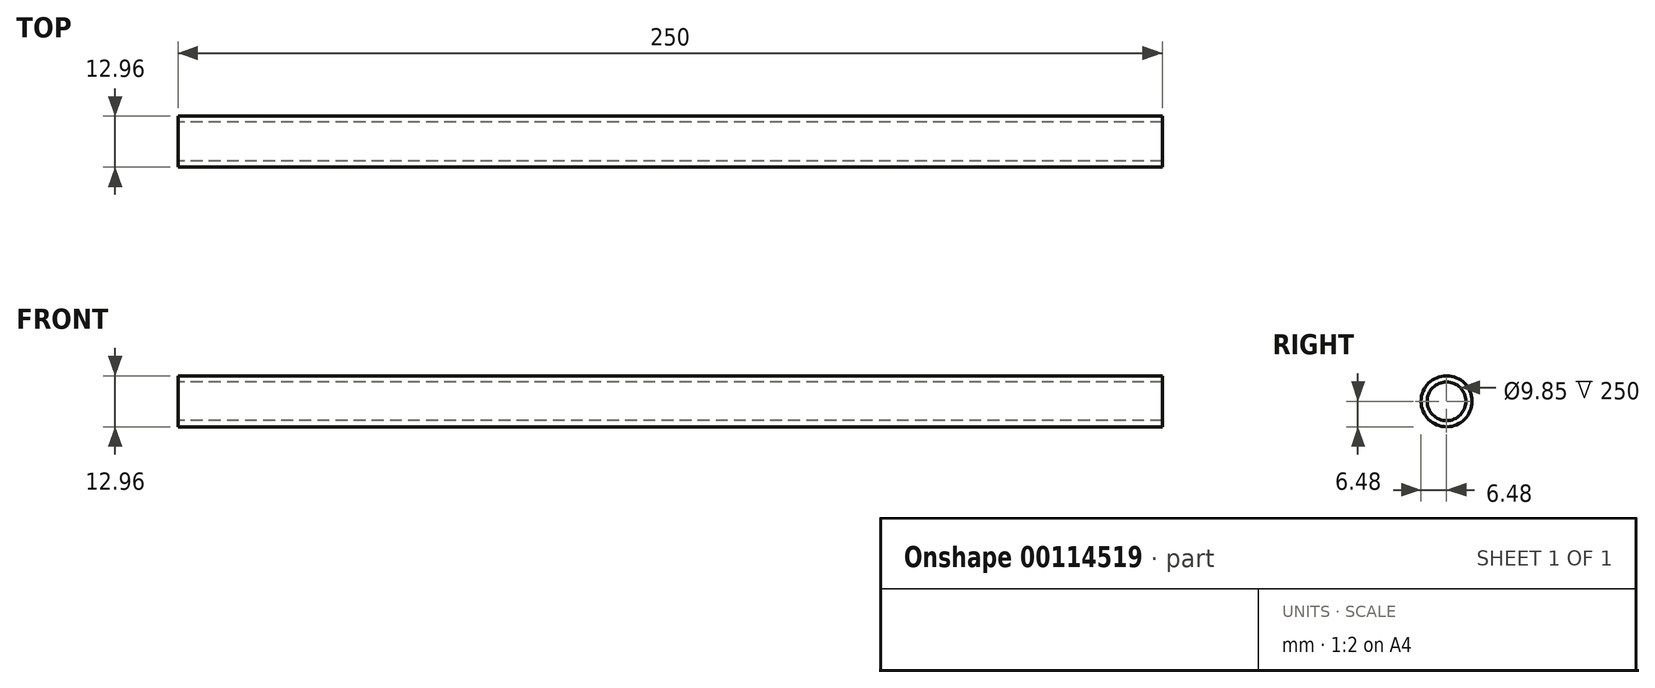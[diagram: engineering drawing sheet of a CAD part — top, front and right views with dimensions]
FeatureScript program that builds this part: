
annotation { "Feature Type Name" : "Feature", "Feature Type Description" : "" }
export const myFeature = defineFeature(function(context is Context, id is Id, definition is map)
    precondition{}
    {
        {
            var Q0;
            Q0=qCreatedBy(makeId("Right.planeOp"),FACE);
            var sketch = newSketch(context, id + "F0", { "sketchPlane" : qUnion([Q0])});
            skCircle(sketch, "E0", {"center": v(0, 0) * mm, "radius": 6.48 * mm});
            skCircle(sketch, "E1", {"center": v(0, 0) * mm, "radius": 4.92 * mm});
            skSolve(sketch);
        }
        {
            var Q0;
            Q0=makeQuery(id+"F0.imprint","IMPRINT",FACE,{"disambiguationData":[TD([[makeQuery(id+"F0.imprint","IMPRINT",EDGE,{"derivedFrom":sQuery(id+"F0.wireOp",EDGE,"E0")}),1.0]])]});
            extrude(context, id + "F1", {"entities" : qUnion([Q0]), "depth" : 250 * mm});
        }
    });
